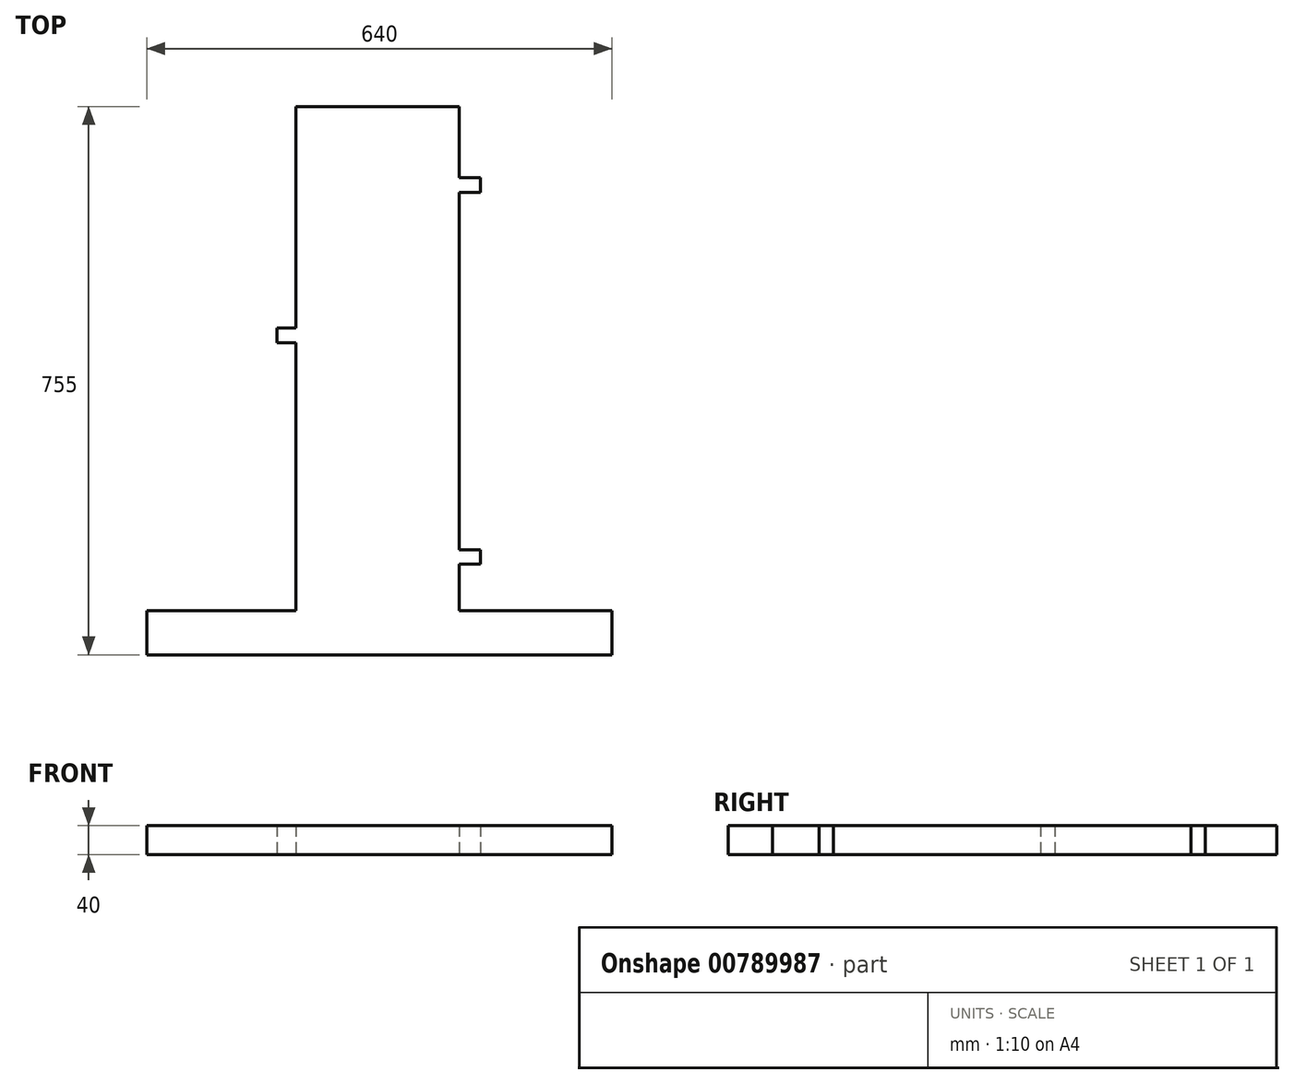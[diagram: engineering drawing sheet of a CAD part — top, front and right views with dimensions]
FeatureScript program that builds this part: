
annotation { "Feature Type Name" : "Feature", "Feature Type Description" : "" }
export const myFeature = defineFeature(function(context is Context, id is Id, definition is map)
    precondition{}
    {
        {
            var Q0;
            Q0=qCreatedBy(makeId("Top.planeOp"),FACE);
            var sketch = newSketch(context, id + "F0", { "sketchPlane" : qUnion([Q0])});
            skLineSegment(sketch, "E0.bottom", {"start": v(0, 0) * mm, "end": v(-640, 0) * mm});
            skLineSegment(sketch, "E0.top", {"start": v(-210, 755) * mm, "end": v(-435, 755) * mm});
            skLineSegment(sketch, "E1", {"start": v(0, 0) * mm, "end": v(0, 61) * mm});
            skLineSegment(sketch, "E2", {"start": v(0, 61) * mm, "end": v(-210, 61) * mm});
            skLineSegment(sketch, "E3", {"start": v(-210, 61) * mm, "end": v(-210, 125) * mm});
            skLineSegment(sketch, "E4", {"start": v(-210, 125) * mm, "end": v(-180.6, 125) * mm});
            skLineSegment(sketch, "E5", {"start": v(-180.6, 125) * mm, "end": v(-180.6, 145) * mm});
            skLineSegment(sketch, "E6", {"start": v(-180.6, 145) * mm, "end": v(-210, 145) * mm});
            skLineSegment(sketch, "E7", {"start": v(-210, 145) * mm, "end": v(-210, 636.85) * mm});
            skLineSegment(sketch, "E8", {"start": v(-210, 636.85) * mm, "end": v(-180.6, 636.85) * mm});
            skLineSegment(sketch, "E9", {"start": v(-180.6, 636.85) * mm, "end": v(-180.6, 656.85) * mm});
            skLineSegment(sketch, "E10", {"start": v(-180.6, 656.85) * mm, "end": v(-210, 656.85) * mm});
            skLineSegment(sketch, "E11", {"start": v(-210, 656.85) * mm, "end": v(-210, 755) * mm});
            skLineSegment(sketch, "E12", {"start": v(-640, 0) * mm, "end": v(-640, 61) * mm});
            skLineSegment(sketch, "E13", {"start": v(-640, 61) * mm, "end": v(-435, 61) * mm});
            skLineSegment(sketch, "E14", {"start": v(-435, 61) * mm, "end": v(-435, 429.95) * mm});
            skLineSegment(sketch, "E15", {"start": v(-435, 429.95) * mm, "end": v(-461, 429.95) * mm});
            skLineSegment(sketch, "E16", {"start": v(-461, 429.95) * mm, "end": v(-461, 449.95) * mm});
            skLineSegment(sketch, "E17", {"start": v(-461, 449.95) * mm, "end": v(-435, 449.95) * mm});
            skLineSegment(sketch, "E18", {"start": v(-435, 449.95) * mm, "end": v(-435, 755) * mm});
            skSolve(sketch);
        }
        {
            var Q0;
            Q0=makeQuery(id+"F0.imprint","IMPRINT",FACE,{"disambiguationData":[TD([[makeQuery(id+"F0.imprint","IMPRINT",EDGE,{"derivedFrom":sQuery(id+"F0.wireOp",EDGE,"E0.bottom")}),-1.0]])]});
            extrude(context, id + "F1", {"entities" : qUnion([Q0]), "depth" : 40 * mm, "offsetDistance" : 25 * mm});
        }
    });
